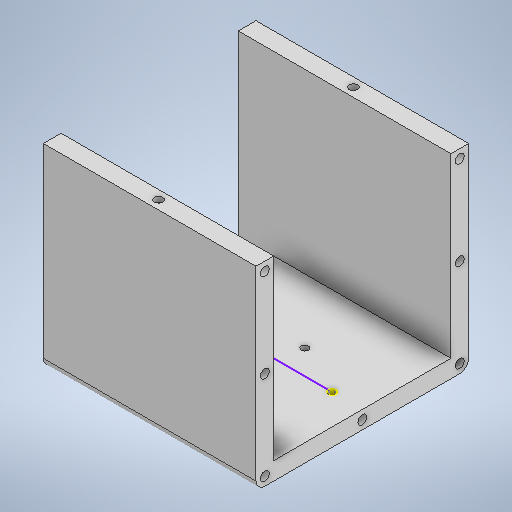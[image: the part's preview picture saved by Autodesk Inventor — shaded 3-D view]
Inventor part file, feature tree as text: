
AUTODESK INVENTOR PART (.ipt)
format: ipt  version: 2025.1 (Build 291241020, 241B)  size: 313,344 bytes
history: native  units: in
note: dims shown in document units (in); Inventor stores cm internally (conversion verified against a paired STEP export)
features: sketch x12, extrude x9, fillet x1
ambient origin geometry x8: Origin, YZ Plane, XZ Plane, XY Plane, X Axis, Y Axis, Z Axis, Center Point
bodies: Solid1 (feature_tree)
feature tree (22):
  sketch  "Sketch1"  dims[d0=6.0in d1=6.0in]
  extrude  "Extrusion1"  Depth=6.0in
  extrude  "Extrusion2"  Depth=0.5in
  fillet  "Fillet1"  Radius=0.5in
  extrude  "Extrusion3"  Depth=0.25in
  sketch  "Sketch5"  dims[d15=6.0in d16=0.2362in]
  extrude  "Extrusion5"  Depth=0.5in TaperAngle=0.0deg
  extrude  "Extrusion6"  Depth=6.0in
  extrude  "Extrusion7"  Depth=0.1575in TaperAngle=0.0deg
  sketch  "Sketch8"  dims[d23=0.25in d24=0.205in]
  sketch  "Sketch9"  dims[d25=3.45in d26=1.4in]
  extrude  "Extrusion8"  Depth=0.5in TaperAngle=0.0deg
  extrude  "Extrusion9"  Depth=0.25in
  extrude  "Extrusion11"  Depth=1.4in
  sketch  "Sketch2"  dims[d2=0.5in d3=0.0in d4=0.5in d5=0.5in]
  sketch  "Sketch3"  dims[d6=5.0in d7=0.0in d8=0.25in]
  sketch  "Sketch4"  dims[d9=5.0in d11=0.5in d12=0.0in]
  sketch  "Sketch6"  dims[d17=0.2362in d18=0.1575in d19=0.0in]
  sketch  "Sketch7"  dims[d20=2.75in d21=0.5in d22=0.0in]
  sketch  "Sketch10"  dims[d27=2.8in]
  sketch  "Sketch11"  dims[d28=0.205in]
  sketch  "Sketch13"  dims[d29=0.205in d30=0.157in d31=0.0in d32=0.45in d33=3.005in d34=0.157in d35=0.0in d36=0.205in d37=0.205in d38=0.205in d39=1.38in d40=1.38in d41=0.205in d42=0.205in d43=0.205in d44=0.205in d45=0.205in d46=1.0in d47=0.0in d52=1.0in d53=0.0in d54=0.205in d55=1.0in d56=0.0in]
